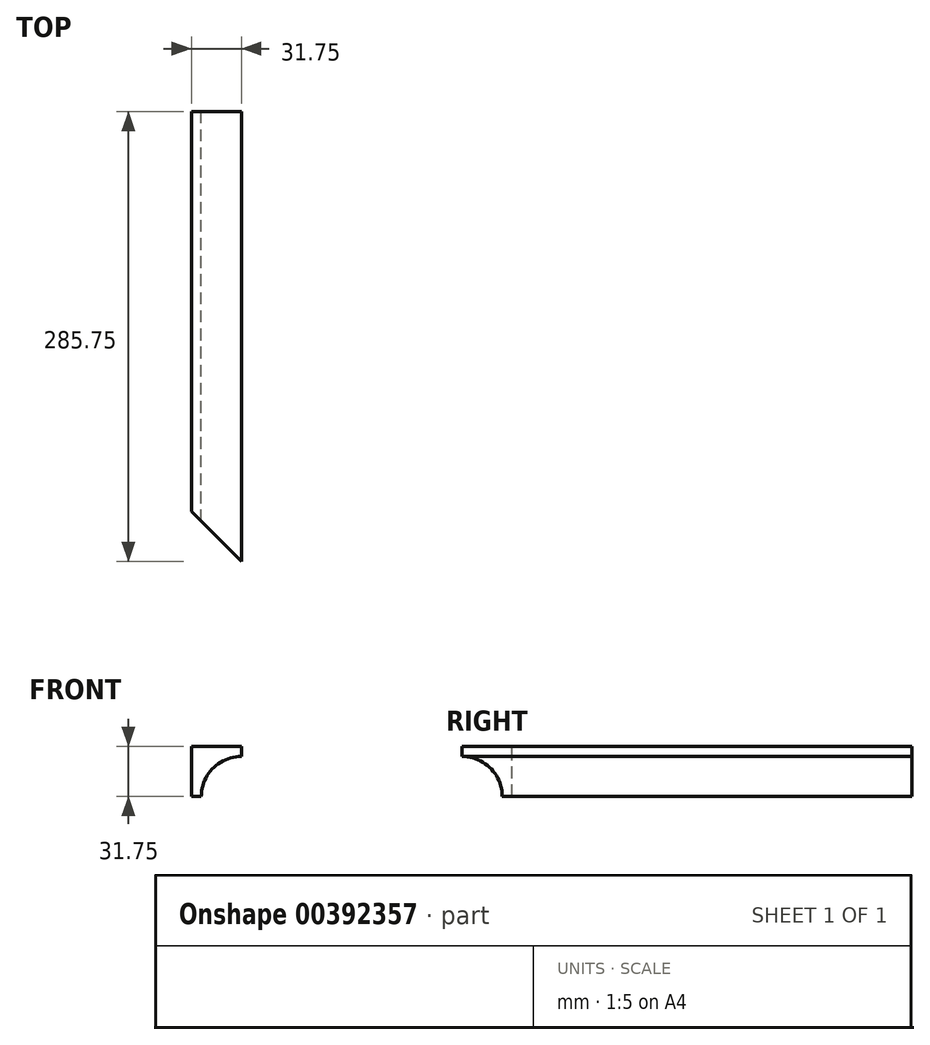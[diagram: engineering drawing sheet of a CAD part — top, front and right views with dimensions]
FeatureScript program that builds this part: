
annotation { "Feature Type Name" : "Feature", "Feature Type Description" : "" }
export const myFeature = defineFeature(function(context is Context, id is Id, definition is map)
    precondition{}
    {
        {
            var Q0;
            Q0=qCreatedBy(makeId("Front.planeOp"),FACE);
            var sketch = newSketch(context, id + "F0", { "sketchPlane" : qUnion([Q0])});
            skLineSegment(sketch, "E0.bottom", {"start": v(0, 0) * mm, "end": v(-31.75, 0) * mm});
            skLineSegment(sketch, "E0.top", {"start": v(0, 31.75) * mm, "end": v(-31.75, 31.75) * mm});
            skLineSegment(sketch, "E0.left", {"start": v(0, 0) * mm, "end": v(0, 31.75) * mm});
            skLineSegment(sketch, "E0.right", {"start": v(-31.75, 0) * mm, "end": v(-31.75, 31.75) * mm});
            skArc(sketch, "E1", {"start": v(-25.4, 0) * mm, "mid": v(-17.96, 17.96) * mm, "end": v(0, 25.4) * mm});
            skSolve(sketch);
        }
        {
            var Q0;
            {var subQ2=sQuery(id+"F0.wireOp",EDGE,"E0.top");Q0=makeQuery(id+"F0.imprint","IMPRINT",FACE,{"disambiguationData":[TD([[makeQuery(id+"F0.imprint","IMPRINT",EDGE,{"derivedFrom":subQ2}),1.0]])]});}
            extrude(context, id + "F1", {"entities" : qUnion([Q0]), "depth" : 285.75 * mm});
        }
        {
            var Q0;
            Q0=makeQuery(id+"F1.opExtrude","SWEPT_FACE",FACE,{"disambiguationData":[OSD([sQuery(id+"F0.wireOp",EDGE,"E0.top")])]});
            var sketch = newSketch(context, id + "F2", { "sketchPlane" : qUnion([Q0])});
            skLineSegment(sketch, "E2", {"start": v(0, -285.75) * mm, "end": v(-31.75, -254) * mm});
            skSolve(sketch);
        }
        {
            var Q0;
            {var subQ0=sQuery(id+"F2.wireOp",EDGE,"E2");Q0=makeQuery(id+"F2.imprint","IMPRINT",FACE,{"disambiguationData":[TD([[makeQuery(id+"F2.imprint","IMPRINT",EDGE,{"derivedFrom":subQ0}),1.0]])]});}
            extrude(context, id + "F3", {"entities" : qUnion([Q0]), "operationType" : NewBodyOperationType.REMOVE, "oppositeDirection" : true, "depth" : 50.8 * mm});
        }
    });
